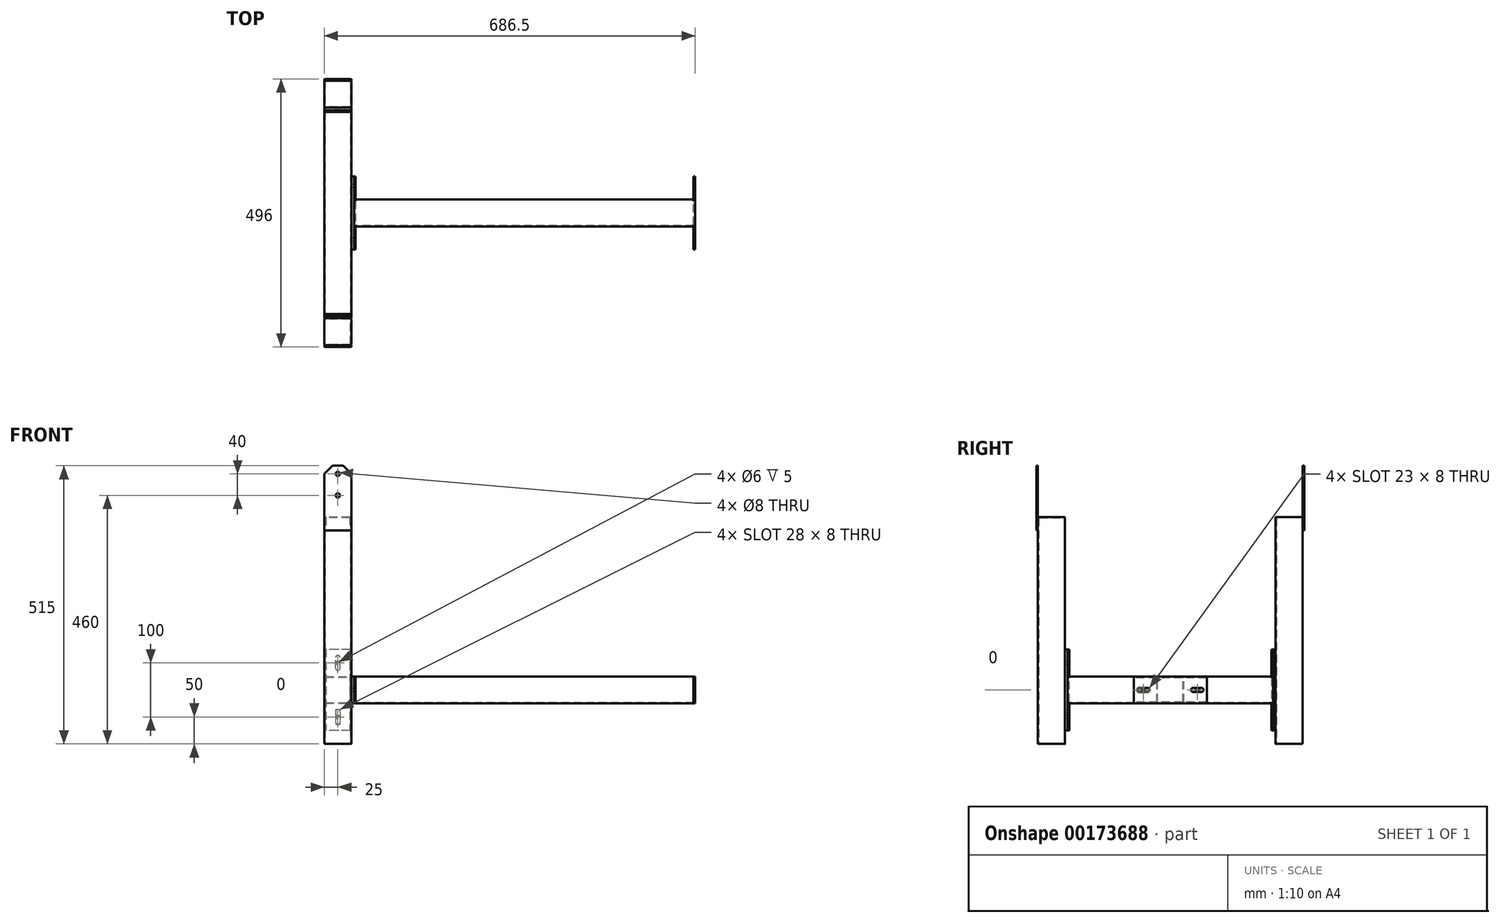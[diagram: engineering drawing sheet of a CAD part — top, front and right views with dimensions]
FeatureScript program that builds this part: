
annotation { "Feature Type Name" : "Feature", "Feature Type Description" : "" }
export const myFeature = defineFeature(function(context is Context, id is Id, definition is map)
    precondition{}
    {
        {
            var Q0;
            Q0=qCreatedBy(makeId("Top.planeOp"),FACE);
            var sketch = newSketch(context, id + "F0", { "sketchPlane" : qUnion([Q0])});
            skLineSegment(sketch, "E0.bottom", {"start": v(22, -25) * mm, "end": v(-22, -25) * mm});
            skLineSegment(sketch, "E0.top", {"start": v(22, 25) * mm, "end": v(-22, 25) * mm});
            skLineSegment(sketch, "E0.left", {"start": v(25, -22) * mm, "end": v(25, 22) * mm});
            skLineSegment(sketch, "E0.right", {"start": v(-25, -22) * mm, "end": v(-25, 22) * mm});
            skPoint(sketch, "E0.middle", {"position": v(0, 0) * mm});
            skPoint(sketch, "E1.visualSharp", {"position": v(-25, 25) * mm});
            skArc(sketch, "E1.filletArc", {"start": v(-22, 25) * mm, "mid": v(-24.12, 24.12) * mm, "end": v(-25, 22) * mm});
            skPoint(sketch, "E2.visualSharp", {"position": v(25, 25) * mm});
            skArc(sketch, "E2.filletArc", {"start": v(25, 22) * mm, "mid": v(24.12, 24.12) * mm, "end": v(22, 25) * mm});
            skPoint(sketch, "E3.visualSharp", {"position": v(25, -25) * mm});
            skArc(sketch, "E3.filletArc", {"start": v(22, -25) * mm, "mid": v(24.12, -24.12) * mm, "end": v(25, -22) * mm});
            skPoint(sketch, "E4.visualSharp", {"position": v(-25, -25) * mm});
            skArc(sketch, "E4.filletArc", {"start": v(-25, -22) * mm, "mid": v(-24.12, -24.12) * mm, "end": v(-22, -25) * mm});
            skArc(sketch, "E5.0", {"start": v(23.5, 22) * mm, "mid": v(23.06, 23.06) * mm, "end": v(22, 23.5) * mm});
            skLineSegment(sketch, "E5.1", {"start": v(23.5, -22) * mm, "end": v(23.5, 22) * mm});
            skLineSegment(sketch, "E5.2", {"start": v(22, 23.5) * mm, "end": v(-22, 23.5) * mm});
            skArc(sketch, "E5.3", {"start": v(22, -23.5) * mm, "mid": v(23.06, -23.06) * mm, "end": v(23.5, -22) * mm});
            skArc(sketch, "E5.4", {"start": v(-22, 23.5) * mm, "mid": v(-23.06, 23.06) * mm, "end": v(-23.5, 22) * mm});
            skLineSegment(sketch, "E5.5", {"start": v(-23.5, -22) * mm, "end": v(-23.5, 22) * mm});
            skArc(sketch, "E5.6", {"start": v(-23.5, -22) * mm, "mid": v(-23.06, -23.06) * mm, "end": v(-22, -23.5) * mm});
            skLineSegment(sketch, "E5.7", {"start": v(22, -23.5) * mm, "end": v(-22, -23.5) * mm});
            skSolve(sketch);
        }
        {
            var Q0;
            Q0=makeQuery(id+"F0.imprint","IMPRINT",FACE,{"disambiguationData":[TD([[makeQuery(id+"F0.imprint","IMPRINT",EDGE,{"derivedFrom":sQuery(id+"F0.wireOp",EDGE,"E0.bottom")}),-1.0]])]});
            extrude(context, id + "F1", {"entities" : qUnion([Q0]), "depth" : 420 * mm});
        }
        {
            var Q0;
            Q0=makeQuery(id+"F1.opExtrude","SWEPT_FACE",FACE,{"disambiguationData":[OSD([sQuery(id+"F0.wireOp",EDGE,"E0.top")])]});
            var sketch = newSketch(context, id + "F2", { "sketchPlane" : qUnion([Q0])});
            skLineSegment(sketch, "E6.bottom", {"start": v(-25, 175) * mm, "end": v(25, 175) * mm});
            skLineSegment(sketch, "E6.top", {"start": v(-25, 25) * mm, "end": v(25, 25) * mm});
            skLineSegment(sketch, "E6.left", {"start": v(-25, 175) * mm, "end": v(-25, 25) * mm});
            skLineSegment(sketch, "E6.right", {"start": v(25, 175) * mm, "end": v(25, 25) * mm});
            skCircle(sketch, "E7", {"center": v(0, 150) * mm, "radius": 3 * mm});
            skCircle(sketch, "E8", {"center": v(0, 50) * mm, "radius": 3 * mm});
            skLineSegment(sketch, "E9", {"start": v(25, 100) * mm, "end": v(-25, 100) * mm, "construction": true});
            skPoint(sketch, "E10.middle", {"position": v(0, 100) * mm});
            skLineSegment(sketch, "E11", {"start": v(0, 125) * mm, "end": v(0, 75) * mm, "construction": true});
            skLineSegment(sketch, "E12", {"start": v(-89.65, -125) * mm, "end": v(137.55, -125) * mm, "construction": true});
            skSolve(sketch);
        }
        {
            var Q0;
            Q0=qSketchRegion(id+"F2",true);
            extrude(context, id + "F3", {"entities" : qUnion([Q0]), "operationType" : NewBodyOperationType.ADD, "depth" : 5 * mm});
        }
        {
            var Q0;
            Q0=makeQuery(id+"F1.opExtrude","CAP_FACE",FACE,{"disambiguationData":[OSD([sQuery(id+"F0.wireOp",EDGE,"E0.bottom"),sQuery(id+"F0.wireOp",EDGE,"E0.top"),sQuery(id+"F0.wireOp",EDGE,"E0.left"),sQuery(id+"F0.wireOp",EDGE,"E0.right"),sQuery(id+"F0.wireOp",EDGE,"E1.filletArc"),sQuery(id+"F0.wireOp",EDGE,"E2.filletArc"),sQuery(id+"F0.wireOp",EDGE,"E3.filletArc"),sQuery(id+"F0.wireOp",EDGE,"E4.filletArc"),sQuery(id+"F0.wireOp",EDGE,"E5.0"),sQuery(id+"F0.wireOp",EDGE,"E5.1"),sQuery(id+"F0.wireOp",EDGE,"E5.2"),sQuery(id+"F0.wireOp",EDGE,"E5.3"),sQuery(id+"F0.wireOp",EDGE,"E5.4"),sQuery(id+"F0.wireOp",EDGE,"E5.5"),sQuery(id+"F0.wireOp",EDGE,"E5.6"),sQuery(id+"F0.wireOp",EDGE,"E5.7")])],"isStart":false});
            var sketch = newSketch(context, id + "F4", { "sketchPlane" : qUnion([Q0])});
            skLineSegment(sketch, "E13.0", {"start": v(-25, -22) * mm, "end": v(-25, 22) * mm});
            skArc(sketch, "E13.1", {"start": v(-25, -22) * mm, "mid": v(-24.12, -24.12) * mm, "end": v(-22, -25) * mm});
            skLineSegment(sketch, "E13.2", {"start": v(22, -25) * mm, "end": v(-22, -25) * mm});
            skArc(sketch, "E13.3", {"start": v(22, -25) * mm, "mid": v(24.12, -24.12) * mm, "end": v(25, -22) * mm});
            skLineSegment(sketch, "E13.4", {"start": v(25, -22) * mm, "end": v(25, 22) * mm});
            skArc(sketch, "E13.5", {"start": v(25, 22) * mm, "mid": v(24.12, 24.12) * mm, "end": v(22, 25) * mm});
            skLineSegment(sketch, "E13.6", {"start": v(22, 25) * mm, "end": v(-22, 25) * mm});
            skArc(sketch, "E13.7", {"start": v(-22, 25) * mm, "mid": v(-24.12, 24.12) * mm, "end": v(-25, 22) * mm});
            skSolve(sketch);
        }
        {
            var Q0;
            Q0=makeQuery(id+"F4.imprint","IMPRINT",FACE,{"disambiguationData":[TD([[makeQuery(id+"F4.imprint","IMPRINT",EDGE,{"derivedFrom":makeQuery(id+"F1.opExtrude","CAP_EDGE",EDGE,{"disambiguationData":[OSD([sQuery(id+"F0.wireOp",EDGE,"E5.0")])],"isStart":false})}),1.0]])]});
            extrude(context, id + "F5", {"entities" : qUnion([Q0]), "operationType" : NewBodyOperationType.ADD, "oppositeDirection" : true, "depth" : 1.5 * mm});
        }
        {
            var Q0;
            Q0=makeQuery(id+"F1.opExtrude","SWEPT_FACE",FACE,{"disambiguationData":[OSD([sQuery(id+"F0.wireOp",EDGE,"E0.bottom")])]});
            var sketch = newSketch(context, id + "F6", { "sketchPlane" : qUnion([Q0])});
            skLineSegment(sketch, "E14.bottom", {"start": v(-25, 515) * mm, "end": v(25, 515) * mm});
            skLineSegment(sketch, "E14.top", {"start": v(-25, 395) * mm, "end": v(25, 395) * mm});
            skLineSegment(sketch, "E14.left", {"start": v(-25, 515) * mm, "end": v(-25, 395) * mm});
            skLineSegment(sketch, "E14.right", {"start": v(25, 515) * mm, "end": v(25, 395) * mm});
            skCircle(sketch, "E15", {"center": v(0, 500) * mm, "radius": 4 * mm});
            skCircle(sketch, "E16", {"center": v(0, 460) * mm, "radius": 4 * mm});
            skSolve(sketch);
        }
        {
            var Q0;
            Q0=qSketchRegion(id+"F6",true);
            extrude(context, id + "F7", {"entities" : qUnion([Q0]), "operationType" : NewBodyOperationType.ADD, "depth" : 3 * mm});
        }
        {
            var Q0;
            Q0=makeQuery(id+"F7.opExtrude","SWEPT_EDGE",EDGE,{"disambiguationData":[OSD([sQuery(id+"F6.wireOp",EDGE,"E14.bottom"),sQuery(id+"F6.wireOp",EDGE,"E14.right")])]});
            var Q1;
            Q1=makeQuery(id+"F7.opExtrude","SWEPT_EDGE",EDGE,{"disambiguationData":[OSD([sQuery(id+"F6.wireOp",EDGE,"E14.bottom"),sQuery(id+"F6.wireOp",EDGE,"E14.left")])]});
            chamfer(context, id + "F8", {"entities" : qUnion([Q0, Q1]), "width" : 15 * mm, "tangentPropagation" : true});
        }
        {
            var Q0;
            Q0=makeQuery(id+"F7.opExtrude","CAP_FACE",FACE,{"disambiguationData":[OSD([sQuery(id+"F6.wireOp",EDGE,"E14.bottom"),sQuery(id+"F6.wireOp",EDGE,"E14.top"),sQuery(id+"F6.wireOp",EDGE,"E14.left"),sQuery(id+"F6.wireOp",EDGE,"E14.right"),sQuery(id+"F6.wireOp",EDGE,"E15"),sQuery(id+"F6.wireOp",EDGE,"E16")])],"isStart":true});
            cPlane(context, id + "F9", {"entities" : qUnion([Q0]), "cplaneType" : CPlaneType.OFFSET, "offset" : 245 * mm, "width" : 150 * mm, "height" : 150 * mm});
        }
        {
            var Q0;
            Q0=makeQuery(id+"F1.opExtrude","SWEPT_BODY",BODY,{"disambiguationData":[OSD([sQuery(id+"F0.wireOp",EDGE,"E0.bottom"),sQuery(id+"F0.wireOp",EDGE,"E0.top"),sQuery(id+"F0.wireOp",EDGE,"E0.left"),sQuery(id+"F0.wireOp",EDGE,"E0.right"),sQuery(id+"F0.wireOp",EDGE,"E1.filletArc"),sQuery(id+"F0.wireOp",EDGE,"E2.filletArc"),sQuery(id+"F0.wireOp",EDGE,"E3.filletArc"),sQuery(id+"F0.wireOp",EDGE,"E4.filletArc"),sQuery(id+"F0.wireOp",EDGE,"E5.0"),sQuery(id+"F0.wireOp",EDGE,"E5.1"),sQuery(id+"F0.wireOp",EDGE,"E5.2"),sQuery(id+"F0.wireOp",EDGE,"E5.3"),sQuery(id+"F0.wireOp",EDGE,"E5.4"),sQuery(id+"F0.wireOp",EDGE,"E5.5"),sQuery(id+"F0.wireOp",EDGE,"E5.6"),sQuery(id+"F0.wireOp",EDGE,"E5.7")])]});
            var Q1;
            Q1=qCreatedBy(id+"F9.planeOp",FACE);
            mirror(context, id + "F10", {"entities" : qUnion([Q0]), "mirrorPlane" : qUnion([Q1])});
        }
        {
            var Q0;
            Q0=makeQuery(id+"F3.opExtrude","CAP_FACE",FACE,{"disambiguationData":[OSD([sQuery(id+"F2.wireOp",EDGE,"E6.bottom"),sQuery(id+"F2.wireOp",EDGE,"E6.top"),sQuery(id+"F2.wireOp",EDGE,"E6.left"),sQuery(id+"F2.wireOp",EDGE,"E6.right"),sQuery(id+"F2.wireOp",EDGE,"E7"),sQuery(id+"F2.wireOp",EDGE,"E8")])],"isStart":false});
            var sketch = newSketch(context, id + "F11", { "sketchPlane" : qUnion([Q0])});
            skLineSegment(sketch, "E17.0", {"start": v(-25, 175) * mm, "end": v(25, 175) * mm});
            skLineSegment(sketch, "E17.1", {"start": v(25, 175) * mm, "end": v(25, 25) * mm});
            skLineSegment(sketch, "E17.2", {"start": v(-25, 175) * mm, "end": v(-25, 25) * mm});
            skLineSegment(sketch, "E17.3", {"start": v(-25, 25) * mm, "end": v(25, 25) * mm});
            skCircle(sketch, "E18.0", {"center": v(0, 150) * mm, "radius": 3 * mm, "construction": true});
            skCircle(sketch, "E18.1", {"center": v(0, 50) * mm, "radius": 3 * mm, "construction": true});
            skLineSegment(sketch, "E19.bottom", {"start": v(4, 140) * mm, "end": v(-4, 140) * mm, "construction": true});
            skLineSegment(sketch, "E19.top", {"start": v(4, 160) * mm, "end": v(-4, 160) * mm, "construction": true});
            skLineSegment(sketch, "E19.left", {"start": v(4, 140) * mm, "end": v(4, 160) * mm});
            skLineSegment(sketch, "E19.right", {"start": v(-4, 140) * mm, "end": v(-4, 160) * mm});
            skLineSegment(sketch, "E20.bottom", {"start": v(-4, 60) * mm, "end": v(4, 60) * mm, "construction": true});
            skLineSegment(sketch, "E20.top", {"start": v(-4, 40) * mm, "end": v(4, 40) * mm, "construction": true});
            skLineSegment(sketch, "E20.left", {"start": v(-4, 60) * mm, "end": v(-4, 40) * mm});
            skLineSegment(sketch, "E20.right", {"start": v(4, 60) * mm, "end": v(4, 40) * mm});
            skArc(sketch, "E21", {"start": v(4, 160) * mm, "mid": v(0, 164) * mm, "end": v(-4, 160) * mm});
            skArc(sketch, "E22", {"start": v(-4, 140) * mm, "mid": v(0, 136) * mm, "end": v(4, 140) * mm});
            skArc(sketch, "E23", {"start": v(4, 60) * mm, "mid": v(0, 64) * mm, "end": v(-4, 60) * mm});
            skArc(sketch, "E24", {"start": v(-4, 40) * mm, "mid": v(0, 36) * mm, "end": v(4, 40) * mm});
            skSolve(sketch);
        }
        {
            var Q0;
            Q0=qSketchRegion(id+"F11",true);
            extrude(context, id + "F12", {"entities" : qUnion([Q0]), "depth" : 3 * mm});
        }
        {
            var Q0;
            Q0=makeQuery(id+"F12.opExtrude","SWEPT_BODY",BODY,{"disambiguationData":[OSD([sQuery(id+"F11.wireOp",EDGE,"E17.0"),sQuery(id+"F11.wireOp",EDGE,"E17.1"),sQuery(id+"F11.wireOp",EDGE,"E17.2"),sQuery(id+"F11.wireOp",EDGE,"E17.3"),sQuery(id+"F11.wireOp",EDGE,"E19.left"),sQuery(id+"F11.wireOp",EDGE,"E19.right"),sQuery(id+"F11.wireOp",EDGE,"E20.left"),sQuery(id+"F11.wireOp",EDGE,"E20.right"),sQuery(id+"F11.wireOp",EDGE,"E21"),sQuery(id+"F11.wireOp",EDGE,"E22"),sQuery(id+"F11.wireOp",EDGE,"E23"),sQuery(id+"F11.wireOp",EDGE,"E24")])]});
            var Q1;
            Q1=qCreatedBy(id+"F9.planeOp",FACE);
            mirror(context, id + "F13", {"entities" : qUnion([Q0]), "mirrorPlane" : qUnion([Q1])});
        }
        {
            var Q0;
            Q0=makeQuery(id+"F12.opExtrude","CAP_FACE",FACE,{"disambiguationData":[OSD([sQuery(id+"F11.wireOp",EDGE,"E17.0"),sQuery(id+"F11.wireOp",EDGE,"E17.1"),sQuery(id+"F11.wireOp",EDGE,"E17.2"),sQuery(id+"F11.wireOp",EDGE,"E17.3"),sQuery(id+"F11.wireOp",EDGE,"E19.left"),sQuery(id+"F11.wireOp",EDGE,"E19.right"),sQuery(id+"F11.wireOp",EDGE,"E20.left"),sQuery(id+"F11.wireOp",EDGE,"E20.right"),sQuery(id+"F11.wireOp",EDGE,"E21"),sQuery(id+"F11.wireOp",EDGE,"E22"),sQuery(id+"F11.wireOp",EDGE,"E23"),sQuery(id+"F11.wireOp",EDGE,"E24")])],"isStart":false});
            var sketch = newSketch(context, id + "F14", { "sketchPlane" : qUnion([Q0])});
            skLineSegment(sketch, "E25", {"start": v(-25, 100) * mm, "end": v(25, 100) * mm, "construction": true});
            skLineSegment(sketch, "E26.bottom", {"start": v(22, 75) * mm, "end": v(-22, 75) * mm});
            skLineSegment(sketch, "E26.top", {"start": v(22, 125) * mm, "end": v(-22, 125) * mm});
            skLineSegment(sketch, "E26.left", {"start": v(25, 78) * mm, "end": v(25, 122) * mm});
            skLineSegment(sketch, "E26.right", {"start": v(-25, 78) * mm, "end": v(-25, 122) * mm});
            skPoint(sketch, "E26.middle", {"position": v(0, 100) * mm});
            skPoint(sketch, "E27.visualSharp", {"position": v(-25, 125) * mm});
            skArc(sketch, "E27.filletArc", {"start": v(-22, 125) * mm, "mid": v(-24.12, 124.12) * mm, "end": v(-25, 122) * mm});
            skPoint(sketch, "E28.visualSharp", {"position": v(25, 125) * mm});
            skArc(sketch, "E28.filletArc", {"start": v(25, 122) * mm, "mid": v(24.12, 124.12) * mm, "end": v(22, 125) * mm});
            skPoint(sketch, "E29.visualSharp", {"position": v(25, 75) * mm});
            skArc(sketch, "E29.filletArc", {"start": v(22, 75) * mm, "mid": v(24.12, 75.88) * mm, "end": v(25, 78) * mm});
            skPoint(sketch, "E30.visualSharp", {"position": v(-25, 75) * mm});
            skArc(sketch, "E30.filletArc", {"start": v(-25, 78) * mm, "mid": v(-24.12, 75.88) * mm, "end": v(-22, 75) * mm});
            skArc(sketch, "E31.0", {"start": v(23.5, 122) * mm, "mid": v(23.06, 123.06) * mm, "end": v(22, 123.5) * mm});
            skLineSegment(sketch, "E31.1", {"start": v(23.5, 78) * mm, "end": v(23.5, 122) * mm});
            skLineSegment(sketch, "E31.2", {"start": v(22, 123.5) * mm, "end": v(-22, 123.5) * mm});
            skArc(sketch, "E31.3", {"start": v(22, 76.5) * mm, "mid": v(23.06, 76.94) * mm, "end": v(23.5, 78) * mm});
            skArc(sketch, "E31.4", {"start": v(-22, 123.5) * mm, "mid": v(-23.06, 123.06) * mm, "end": v(-23.5, 122) * mm});
            skLineSegment(sketch, "E31.5", {"start": v(-23.5, 78) * mm, "end": v(-23.5, 122) * mm});
            skArc(sketch, "E31.6", {"start": v(-23.5, 78) * mm, "mid": v(-23.06, 76.94) * mm, "end": v(-22, 76.5) * mm});
            skLineSegment(sketch, "E31.7", {"start": v(22, 76.5) * mm, "end": v(-22, 76.5) * mm});
            skSolve(sketch);
        }
        {
            var Q0;
            Q0=qSketchRegion(id+"F14",true);
            extrude(context, id + "F15", {"entities" : qUnion([Q0]), "operationType" : NewBodyOperationType.ADD, "endBound" : BoundingType.UP_TO_NEXT, "depth" : 25 * mm});
        }
        {
            var Q0;
            Q0=makeQuery(id+"F1.opExtrude","SWEPT_FACE",FACE,{"disambiguationData":[OSD([sQuery(id+"F0.wireOp",EDGE,"E0.left")])]});
            cPlane(context, id + "F16", {"entities" : qUnion([Q0]), "cplaneType" : CPlaneType.OFFSET, "offset" : 320.75 * mm, "width" : 150 * mm, "height" : 150 * mm});
        }
        {
            var Q0;
            {var subQ0=makeQuery(id+"F12.opExtrude","SWEPT_FACE",FACE,{"disambiguationData":[OSD([sQuery(id+"F11.wireOp",EDGE,"E17.2")])]});Q0=makeQuery(id+"F15.boolean.opBoolean","MERGE",FACE,{"derivedFrom":[subQ0,makeQuery(id+"F13.opPattern","COPY",FACE,{"derivedFrom":subQ0,"instanceName":"1"}),makeQuery(id+"F15.opExtrude","SWEPT_FACE",FACE,{"disambiguationData":[OSD([sQuery(id+"F14.wireOp",EDGE,"E26.right")])]})]});}
            var sketch = newSketch(context, id + "F17", { "sketchPlane" : qUnion([Q0])});
            skLineSegment(sketch, "E32.bottom", {"start": v(152.5, 125) * mm, "end": v(287.5, 125) * mm});
            skLineSegment(sketch, "E32.top", {"start": v(152.5, 75) * mm, "end": v(287.5, 75) * mm});
            skLineSegment(sketch, "E32.left", {"start": v(152.5, 125) * mm, "end": v(152.5, 75) * mm});
            skLineSegment(sketch, "E32.right", {"start": v(287.5, 125) * mm, "end": v(287.5, 75) * mm});
            skLineSegment(sketch, "E33", {"start": v(287.5, 100) * mm, "end": v(152.5, 100) * mm, "construction": true});
            skPoint(sketch, "E34.middle", {"position": v(220, 100) * mm});
            skLineSegment(sketch, "E35", {"start": v(220, 122) * mm, "end": v(220, 78) * mm, "construction": true});
            skCircle(sketch, "E36", {"center": v(170, 100) * mm, "radius": 3 * mm});
            skCircle(sketch, "E37.MirrorC", {"center": v(270, 100) * mm, "radius": 3 * mm});
            skSolve(sketch);
        }
        {
            var Q0;
            Q0=qSketchRegion(id+"F17",true);
            extrude(context, id + "F18", {"entities" : qUnion([Q0]), "operationType" : NewBodyOperationType.ADD, "depth" : 5 * mm});
        }
        {
            var Q0;
            Q0=makeQuery(id+"F18.opExtrude","CAP_FACE",FACE,{"disambiguationData":[OSD([sQuery(id+"F17.wireOp",EDGE,"E32.bottom"),sQuery(id+"F17.wireOp",EDGE,"E32.top"),sQuery(id+"F17.wireOp",EDGE,"E32.left"),sQuery(id+"F17.wireOp",EDGE,"E32.right"),sQuery(id+"F17.wireOp",EDGE,"E36"),sQuery(id+"F17.wireOp",EDGE,"E37.MirrorC")])],"isStart":false});
            var sketch = newSketch(context, id + "F19", { "sketchPlane" : qUnion([Q0])});
            skLineSegment(sketch, "E38.0", {"start": v(152.5, 125) * mm, "end": v(287.5, 125) * mm});
            skLineSegment(sketch, "E38.1", {"start": v(152.5, 125) * mm, "end": v(152.5, 75) * mm});
            skLineSegment(sketch, "E38.2", {"start": v(152.5, 75) * mm, "end": v(287.5, 75) * mm});
            skLineSegment(sketch, "E38.3", {"start": v(287.5, 125) * mm, "end": v(287.5, 75) * mm});
            skCircle(sketch, "E38.4", {"center": v(270, 100) * mm, "radius": 3 * mm, "construction": true});
            skCircle(sketch, "E38.5", {"center": v(170, 100) * mm, "radius": 3 * mm, "construction": true});
            skCircle(sketch, "E39", {"center": v(170, 100) * mm, "radius": 4 * mm});
            skCircle(sketch, "E40", {"center": v(270, 100) * mm, "radius": 4 * mm});
            skSolve(sketch);
        }
        {
            var Q0;
            Q0=qSketchRegion(id+"F19",true);
            extrude(context, id + "F20", {"entities" : qUnion([Q0]), "depth" : 3 * mm});
        }
        {
            var Q0;
            Q0=makeQuery(id+"F20.opExtrude","SWEPT_BODY",BODY,{"disambiguationData":[OSD([sQuery(id+"F19.wireOp",EDGE,"E38.0"),sQuery(id+"F19.wireOp",EDGE,"E38.1"),sQuery(id+"F19.wireOp",EDGE,"E38.2"),sQuery(id+"F19.wireOp",EDGE,"E38.3"),sQuery(id+"F19.wireOp",EDGE,"E39"),sQuery(id+"F19.wireOp",EDGE,"E40")])]});
            var Q1;
            Q1=qCreatedBy(id+"F16.planeOp",FACE);
            mirror(context, id + "F21", {"entities" : qUnion([Q0]), "mirrorPlane" : qUnion([Q1])});
        }
        {
            var Q0;
            Q0=makeQuery(id+"F20.opExtrude","CAP_FACE",FACE,{"disambiguationData":[OSD([sQuery(id+"F19.wireOp",EDGE,"E38.0"),sQuery(id+"F19.wireOp",EDGE,"E38.1"),sQuery(id+"F19.wireOp",EDGE,"E38.2"),sQuery(id+"F19.wireOp",EDGE,"E38.3"),sQuery(id+"F19.wireOp",EDGE,"E39"),sQuery(id+"F19.wireOp",EDGE,"E40")])],"isStart":false});
            var sketch = newSketch(context, id + "F22", { "sketchPlane" : qUnion([Q0])});
            skLineSegment(sketch, "E41", {"start": v(203.38, 100) * mm, "end": v(236.62, 100) * mm, "construction": true});
            skLineSegment(sketch, "E42.bottom", {"start": v(242, 75) * mm, "end": v(198, 75) * mm});
            skLineSegment(sketch, "E42.top", {"start": v(242, 125) * mm, "end": v(198, 125) * mm});
            skLineSegment(sketch, "E42.left", {"start": v(245, 78) * mm, "end": v(245, 122) * mm});
            skLineSegment(sketch, "E42.right", {"start": v(195, 78) * mm, "end": v(195, 122) * mm});
            skPoint(sketch, "E42.middle", {"position": v(220, 100) * mm});
            skPoint(sketch, "E43.visualSharp", {"position": v(195, 125) * mm});
            skArc(sketch, "E43.filletArc", {"start": v(198, 125) * mm, "mid": v(195.88, 124.12) * mm, "end": v(195, 122) * mm});
            skPoint(sketch, "E44.visualSharp", {"position": v(245, 125) * mm});
            skArc(sketch, "E44.filletArc", {"start": v(245, 122) * mm, "mid": v(244.12, 124.12) * mm, "end": v(242, 125) * mm});
            skPoint(sketch, "E45.visualSharp", {"position": v(245, 75) * mm});
            skArc(sketch, "E45.filletArc", {"start": v(242, 75) * mm, "mid": v(244.12, 75.88) * mm, "end": v(245, 78) * mm});
            skPoint(sketch, "E46.visualSharp", {"position": v(195, 75) * mm});
            skArc(sketch, "E46.filletArc", {"start": v(195, 78) * mm, "mid": v(195.88, 75.88) * mm, "end": v(198, 75) * mm});
            skArc(sketch, "E47.0", {"start": v(243.5, 122) * mm, "mid": v(243.06, 123.06) * mm, "end": v(242, 123.5) * mm});
            skLineSegment(sketch, "E47.1", {"start": v(243.5, 78) * mm, "end": v(243.5, 122) * mm});
            skLineSegment(sketch, "E47.2", {"start": v(242, 123.5) * mm, "end": v(198, 123.5) * mm});
            skArc(sketch, "E47.3", {"start": v(242, 76.5) * mm, "mid": v(243.06, 76.94) * mm, "end": v(243.5, 78) * mm});
            skArc(sketch, "E47.4", {"start": v(198, 123.5) * mm, "mid": v(196.94, 123.06) * mm, "end": v(196.5, 122) * mm});
            skLineSegment(sketch, "E47.5", {"start": v(196.5, 78) * mm, "end": v(196.5, 122) * mm});
            skArc(sketch, "E47.6", {"start": v(196.5, 78) * mm, "mid": v(196.94, 76.94) * mm, "end": v(198, 76.5) * mm});
            skLineSegment(sketch, "E47.7", {"start": v(242, 76.5) * mm, "end": v(198, 76.5) * mm});
            skLineSegment(sketch, "E48", {"start": v(220, 100) * mm, "end": v(220, 125) * mm, "construction": true});
            skSolve(sketch);
        }
        {
            var Q0;
            Q0=qSketchRegion(id+"F22",true);
            extrude(context, id + "F23", {"entities" : qUnion([Q0]), "operationType" : NewBodyOperationType.ADD, "endBound" : BoundingType.UP_TO_NEXT, "depth" : 25 * mm});
        }
        {
            var Q0;
            Q0=makeQuery(id+"F21.opPattern","COPY",FACE,{"derivedFrom":makeQuery(id+"F20.opExtrude","CAP_FACE",FACE,{"disambiguationData":[OSD([sQuery(id+"F19.wireOp",EDGE,"E38.0"),sQuery(id+"F19.wireOp",EDGE,"E38.1"),sQuery(id+"F19.wireOp",EDGE,"E38.2"),sQuery(id+"F19.wireOp",EDGE,"E38.3"),sQuery(id+"F19.wireOp",EDGE,"E39"),sQuery(id+"F19.wireOp",EDGE,"E40")])],"isStart":true}),"instanceName":"1"});
            var sketch = newSketch(context, id + "F24", { "sketchPlane" : qUnion([Q0])});
            skLineSegment(sketch, "E49.bottom", {"start": v(177.5, 96) * mm, "end": v(162.5, 96) * mm});
            skLineSegment(sketch, "E49.top", {"start": v(177.5, 104) * mm, "end": v(162.5, 104) * mm});
            skLineSegment(sketch, "E49.left", {"start": v(177.5, 96) * mm, "end": v(177.5, 104) * mm, "construction": true});
            skLineSegment(sketch, "E49.right", {"start": v(162.5, 96) * mm, "end": v(162.5, 104) * mm, "construction": true});
            skPoint(sketch, "E49.middle", {"position": v(170, 100) * mm});
            skLineSegment(sketch, "E50", {"start": v(220, 125) * mm, "end": v(220, 75) * mm, "construction": true});
            skArc(sketch, "E51", {"start": v(162.5, 104) * mm, "mid": v(158.5, 100) * mm, "end": v(162.5, 96) * mm});
            skArc(sketch, "E52", {"start": v(177.5, 96) * mm, "mid": v(181.5, 100) * mm, "end": v(177.5, 104) * mm});
            skArc(sketch, "E53.MirrorCS", {"start": v(262.5, 96) * mm, "mid": v(258.5, 100) * mm, "end": v(262.5, 104) * mm});
            skLineSegment(sketch, "E54.MirrorCS", {"start": v(262.5, 104) * mm, "end": v(277.5, 104) * mm});
            skArc(sketch, "E55.MirrorCS", {"start": v(277.5, 104) * mm, "mid": v(281.5, 100) * mm, "end": v(277.5, 96) * mm});
            skLineSegment(sketch, "E56.MirrorCS", {"start": v(262.5, 96) * mm, "end": v(277.5, 96) * mm});
            skSolve(sketch);
        }
        {
            var Q0;
            Q0=qSketchRegion(id+"F24",true);
            extrude(context, id + "F25", {"entities" : qUnion([Q0]), "operationType" : NewBodyOperationType.REMOVE, "endBound" : BoundingType.UP_TO_NEXT, "oppositeDirection" : true, "depth" : 25 * mm});
        }
    });
